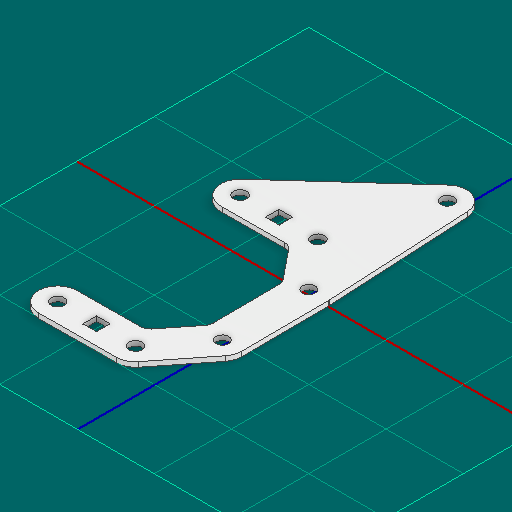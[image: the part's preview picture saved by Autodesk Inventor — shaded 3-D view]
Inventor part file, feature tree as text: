
AUTODESK INVENTOR PART (.ipt)
format: ipt  version: 2025 (Build 290162000, 162)  size: 186,880 bytes
history: native  units: in
note: dims shown in document units (in); Inventor stores cm internally (conversion verified against a paired STEP export)
features: other x6, sketch x1
ambient origin geometry x8: Origin, YZ Plane, XZ Plane, XY Plane, X Axis, Y Axis, Z Axis, Center Point
bodies: Solid1 (feature_tree)
feature tree (7):
  other  "funnel_gusset.ipt"
  other  "Blocks"
  other  "main_gusset"
  other  "Solid1::funnel_gusset.ipt"
  other  "TaggingFeature1"
  sketch  "Sketch1"  dims[d0=0.3937in d1=0.5in d2=0.5in d3=0.125in d6=0.176in d7=0.176in d8=0.176in d9=0.176in d10=0.5in d11=0.5in d12=0.25in d13=0.25in d14=0.625in d15=0.625in d16=0.5in]
  other  "main_gusset:1"
